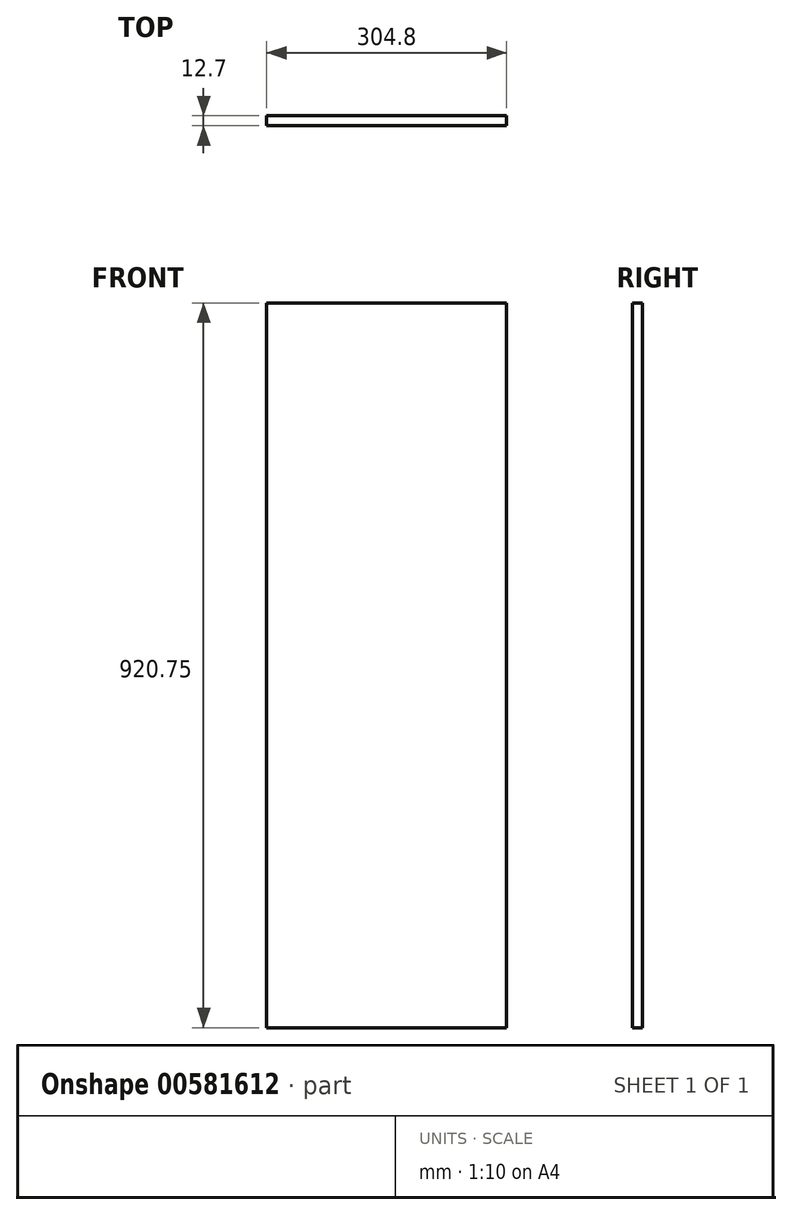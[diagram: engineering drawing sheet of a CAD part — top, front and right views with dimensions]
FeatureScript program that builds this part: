
annotation { "Feature Type Name" : "Feature", "Feature Type Description" : "" }
export const myFeature = defineFeature(function(context is Context, id is Id, definition is map)
    precondition{}
    {
        {
            var Q0;
            Q0=qCreatedBy(makeId("Front.planeOp"),FACE);
            var sketch = newSketch(context, id + "F0", { "sketchPlane" : qUnion([Q0])});
            skLineSegment(sketch, "E0.bottom", {"start": v(-151.31, 106.18) * mm, "end": v(153.49, 106.18) * mm});
            skLineSegment(sketch, "E0.top", {"start": v(-151.31, -104.76) * mm, "end": v(153.49, -104.76) * mm});
            skLineSegment(sketch, "E0.left", {"start": v(-151.31, 106.18) * mm, "end": v(-151.31, -104.76) * mm});
            skLineSegment(sketch, "E0.right", {"start": v(153.49, 106.18) * mm, "end": v(153.49, -104.76) * mm});
            skSolve(sketch);
        }
        {
            var Q0;
            Q0=makeQuery(id+"F0.imprint","IMPRINT",FACE,{"disambiguationData":[TD([[makeQuery(id+"F0.imprint","IMPRINT",EDGE,{"derivedFrom":sQuery(id+"F0.wireOp",EDGE,"E0.bottom")}),-1.0]])]});
            var sketch = newSketch(context, id + "F1", { "sketchPlane" : qUnion([Q0])});
            skLineSegment(sketch, "E1.bottom", {"start": v(-232.71, 439.2) * mm, "end": v(72.09, 439.2) * mm});
            skLineSegment(sketch, "E1.top", {"start": v(-232.71, -481.54) * mm, "end": v(72.09, -481.54) * mm});
            skLineSegment(sketch, "E1.left", {"start": v(-232.71, 439.2) * mm, "end": v(-232.71, -481.54) * mm});
            skLineSegment(sketch, "E1.right", {"start": v(72.09, 439.2) * mm, "end": v(72.09, -481.54) * mm});
            skSolve(sketch);
        }
        {
            var Q0;
            Q0 = qSketchRegion(id + "F1", true);
            extrude(context, id + "F2", {"entities" : qUnion([Q0]), "depth" : 12.7 * mm, "offsetDistance" : 25.4 * mm});
        }
    });
